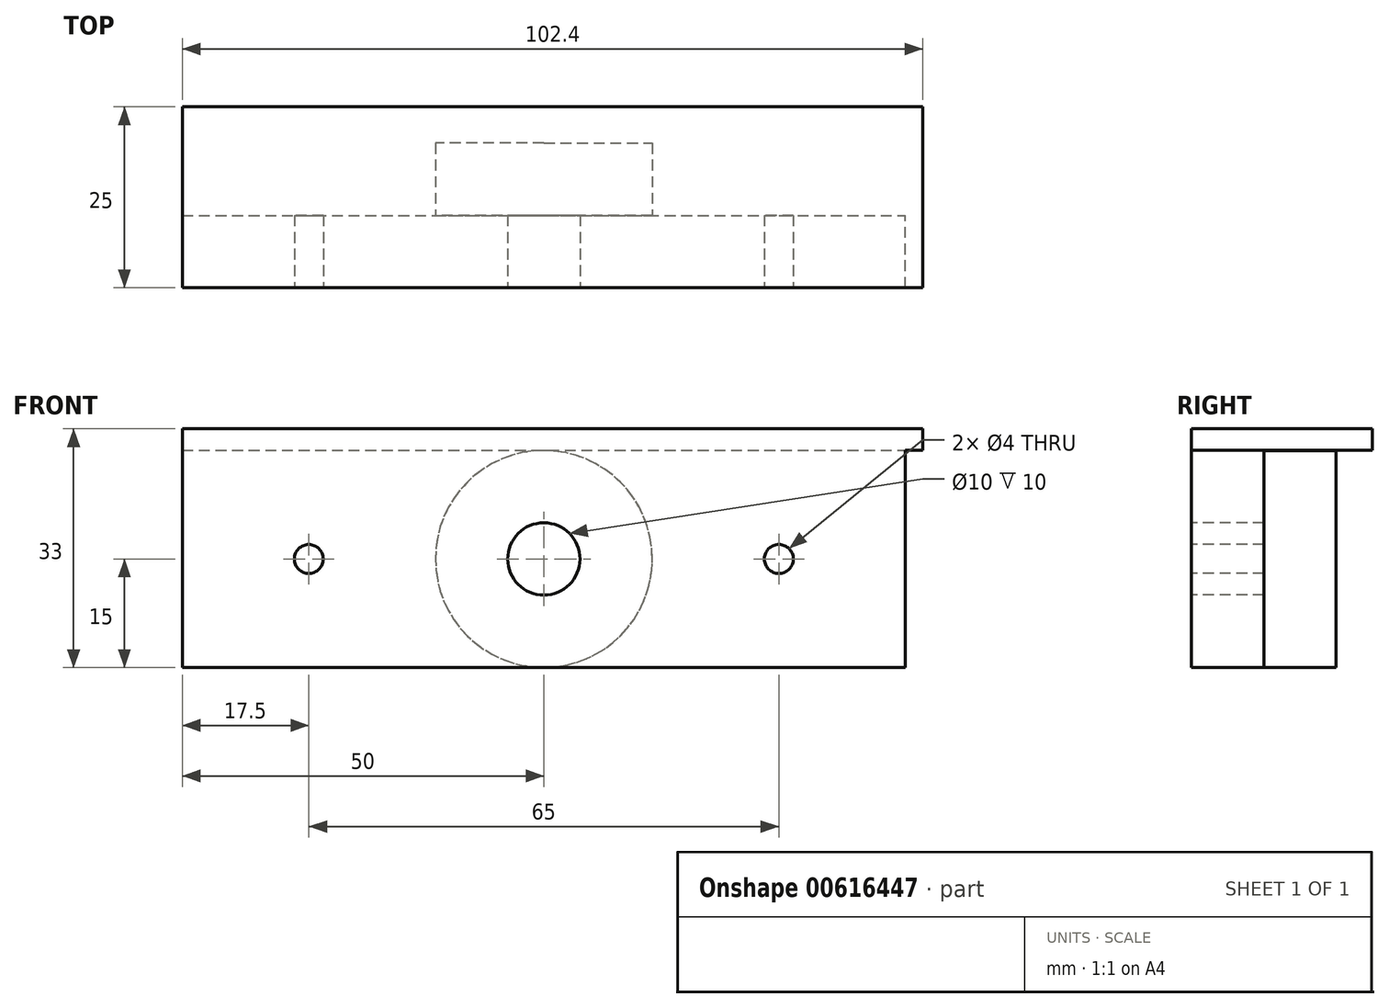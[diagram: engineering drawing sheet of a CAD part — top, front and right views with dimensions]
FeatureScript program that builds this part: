
annotation { "Feature Type Name" : "Feature", "Feature Type Description" : "" }
export const myFeature = defineFeature(function(context is Context, id is Id, definition is map)
    precondition{}
    {
        {
            var Q0;
            Q0=qCreatedBy(makeId("Front.planeOp"),FACE);
            var sketch = newSketch(context, id + "F0", { "sketchPlane" : qUnion([Q0])});
            skLineSegment(sketch, "E0.bottom", {"start": v(-50, -15) * mm, "end": v(50, -15) * mm});
            skLineSegment(sketch, "E0.top", {"start": v(-50, 15) * mm, "end": v(50, 15) * mm});
            skLineSegment(sketch, "E0.left", {"start": v(-50, -15) * mm, "end": v(-50, 15) * mm});
            skLineSegment(sketch, "E0.right", {"start": v(50, -15) * mm, "end": v(50, 15) * mm});
            skPoint(sketch, "E0.middle", {"position": v(0, 0) * mm});
            skSolve(sketch);
        }
        {
            var Q0;
            Q0 = qSketchRegion(id + "F0", true);
            extrude(context, id + "F1", {"entities" : qUnion([Q0]), "depth" : 10 * mm, "offsetDistance" : 25 * mm});
        }
        {
            var Q0;
            Q0=makeQuery(id+"F1.opExtrude","CAP_FACE",FACE,{"disambiguationData":[OSD([sQuery(id+"F0.wireOp",EDGE,"E0.bottom"),sQuery(id+"F0.wireOp",EDGE,"E0.top"),sQuery(id+"F0.wireOp",EDGE,"E0.left"),sQuery(id+"F0.wireOp",EDGE,"E0.right")])],"isStart":false});
            var sketch = newSketch(context, id + "F2", { "sketchPlane" : qUnion([Q0])});
            skCircle(sketch, "E1", {"center": v(-32.5, 0) * mm, "radius": 2 * mm});
            skCircle(sketch, "E2.MirrorC", {"center": v(32.5, 0) * mm, "radius": 2 * mm});
            skCircle(sketch, "E3", {"center": v(0, 0) * mm, "radius": 5 * mm});
            skSolve(sketch);
        }
        {
            var Q0;
            Q0 = qSketchRegion(id + "F2", true);
            extrude(context, id + "F3", {"entities" : qUnion([Q0]), "operationType" : NewBodyOperationType.REMOVE, "oppositeDirection" : true, "depth" : 25 * mm, "offsetDistance" : 25 * mm});
        }
        {
            var Q0;
            Q0=makeQuery(id+"F1.opExtrude","SWEPT_FACE",FACE,{"disambiguationData":[OSD([sQuery(id+"F0.wireOp",EDGE,"E0.top")])]});
            var sketch = newSketch(context, id + "F4", { "sketchPlane" : qUnion([Q0])});
            skLineSegment(sketch, "E4.bottom", {"start": v(-50, -10) * mm, "end": v(52.4, -10) * mm});
            skLineSegment(sketch, "E4.top", {"start": v(-50, 15) * mm, "end": v(52.4, 15) * mm});
            skLineSegment(sketch, "E4.left", {"start": v(-50, -10) * mm, "end": v(-50, 15) * mm});
            skLineSegment(sketch, "E4.right", {"start": v(52.4, -10) * mm, "end": v(52.4, 15) * mm});
            skSolve(sketch);
        }
        {
            var Q0;
            Q0 = qSketchRegion(id + "F4", true);
            extrude(context, id + "F5", {"entities" : qUnion([Q0]), "operationType" : NewBodyOperationType.ADD, "depth" : 3 * mm, "offsetDistance" : 25 * mm});
        }
        {
            var Q0;
            Q0=makeQuery(id+"F1.opExtrude","CAP_FACE",FACE,{"disambiguationData":[OSD([sQuery(id+"F0.wireOp",EDGE,"E0.bottom"),sQuery(id+"F0.wireOp",EDGE,"E0.top"),sQuery(id+"F0.wireOp",EDGE,"E0.left"),sQuery(id+"F0.wireOp",EDGE,"E0.right")])],"isStart":true});
            var sketch = newSketch(context, id + "F6", { "sketchPlane" : qUnion([Q0])});
            skPoint(sketch, "E5.middle", {"position": v(0, 0) * mm});
            skCircle(sketch, "E6", {"center": v(0, 0) * mm, "radius": 15 * mm});
            skSolve(sketch);
        }
        {
            var Q0;
            Q0 = qSketchRegion(id + "F6", true);
            extrude(context, id + "F7", {"entities" : qUnion([Q0]), "operationType" : NewBodyOperationType.ADD, "depth" : 10 * mm, "offsetDistance" : 25 * mm});
        }
    });
